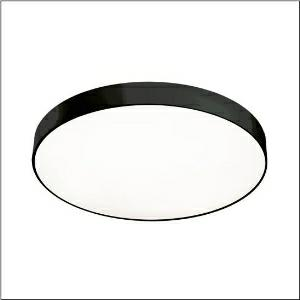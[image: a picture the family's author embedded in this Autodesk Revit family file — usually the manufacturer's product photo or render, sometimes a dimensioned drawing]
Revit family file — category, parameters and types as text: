
# Revit family: round_21_l_51mr38fd0321b
name_source: partatom
category: Lighting Fixtures
units: mm (PartAtom-declared; Revit-internal decimal feet)

## family parameters
Cut with Voids When Loaded = No
Host = Face
Light Source = No
Part Type = Normal
Room Calculation Point = No
Round Connector Dimension = Use Diameter
Shared = No

## types (1)
- Round 21 L (1 x LED, 13590 lm, 97 W, 3000K)
    Apparent Load = 97 VA
    CIE Flux Codes = 49 80 96 100 100
    Color Rendering = 80
    Color Temperature = 3000K
    Default Elevation = 1800 mm
    Description = Round 21 L, wall and ceiling luminaire, primary optical cover: cover, of PMMA, opal, light emission: direct distribution, primary light characteristic: symmetric, installation type: suspended mounting, surface-mounted, LED, rated luminous flux: 13.590lm, luminous efficacy: 140lm/W, light colour: 830, colour temperature: 3000K, control gear: DALI 2, with terminal, 5-pole, mains connection: 230V, AC, 50/60Hz, rated input power: 97W, housing, of aluminium, coated, black, diameter: 850mm, height: 62mm, protection rating (complete): IP40, insulation class (complete): insulation class I (protective earthing), certification: CE, impact resistance: IK04, permissible operating ambient temperature: -10..+35°C, packaging unit: 1 piece
    Height = 87 mm
    Lamp = 1 x LED
    Lamp Light Flux = 13590 lm
    Lamp Power = 97 W
    Lamp count = 1
    Length = 850 mm
    Luminous efficacy = 140 lm/W
    Manufacturer = Siteco
    ModVariant = No
    Model = 51MR38FD0321B
    Mounting Place = Ceiling
    Mounting Type = Surface mounted
    Number of Poles = 1
    OnlyDefault = Yes
    Power Factor = 1
    Product Name = Round 21 L
    Product group = wall and ceiling luminaire | ceiling mounted
    ProductGroupID = 304
    Protection Class = Protection class I
    Protection Degree = IP 40
    RLX_Detail_Level = 1
    RLX_Emergency_Light_Flux = 0 lm
    RLX_Emergency_Type = 0
    RLX_Emergency_Type_DB = No
    RlxData = <blob elided: 23933 chars, md5=56882aca>
    Socket = socket
    Standby Power = 0 W
    System Light Flux = 13590 lm
    System Power = 97 W
    Type Comments = Product without accessories
    Type Image = l_1258328.jpg
    URL = http://relux.com
    VarID = ---
    Voltage = 0 V
    Weight = 0.00 kg
    Width = 0 mm  [stored 0 ft]

note: [stored X ft] marks values corroborated as IEEE doubles in the binary element streams (Revit-internal decimal feet)

## geometry (parser evidence)
native form markers: Blend x4, Sweep x10
no freeform markers — native parametric forms only
